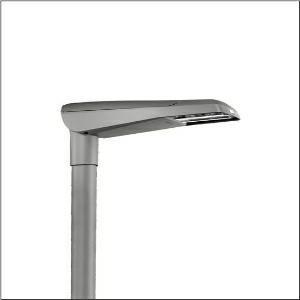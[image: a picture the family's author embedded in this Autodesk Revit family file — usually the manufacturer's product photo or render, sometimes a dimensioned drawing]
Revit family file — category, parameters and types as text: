
# Revit family: streetlight_sl_11_iq_micro___st1_2a_5xc1a41f08ce_4ecf
name_source: partatom
category: Lighting Fixtures
units: mm (PartAtom-declared; Revit-internal decimal feet)

## family parameters
Cut with Voids When Loaded = No
Host = Face
Light Source = No
Part Type = Normal
Room Calculation Point = No
Round Connector Dimension = Use Diameter
Shared = No

## types (1)
- --- (1 x LED, 1960 lm, 12.6 W, 4000K)
    Apparent Load = 13 VA
    CIE Flux Codes = 33 71 96 100 100
    Color Rendering = 70
    Color Temperature = 4000K
    Default Elevation = 1800 mm
    Description = Streetlight SL 11 iQ micro, mast luminaire, primary light control with 3 zone facetted reflector, of plastic, silver coated, highly specular, primary optical cover: cover, of PMMA, transparent, light distribution: ST1.2a, light emission: direct distribution, primary light characteristic: asymmetric, installation type: post-top, side-entry, lamps: LED, High Power LED, rated values: 1.960lm | 12,6W | 155,6lm/W (begin service life); end service life: 1.960lm | 12,9W; at 50% lumin. flux: 980lm | 6,8W | 144,1lm/W, colour temperature: 4000K, colour rendering: CRI > 70, light colour: 740, light setting 1 begin service life: 100% | 1.960lm | 12,6W | 155,6lm/W | 4.000K, light setting 1 end service life: 12,9W, further light settings possible, control: Street-Remote, optimised constant luminous flux control (CLO 2.0), Desk-Remote (wireless, voltage-free reading and setting of iQ features in the workshop via application-optimized NFC function/RFID function), Light-Fading, Smart-Wire, Night-Set, Lumen-Switch, Temp-Guard, Auto-Match, with cable H07RN-F 5x 1.5mm², mains connection: 230..240V, AC, 50/60Hz, connection cable pre-assembled, cable length: 5,5m, luminaire housing, of diecast aluminium, powder-coated, Siteco® metallic grey (DB 702S), please order mast flange separately, inclination adjustable without tools: 0°, 5°, 10°, 15° (post-top) | 0°, -5°, -10°, -15° (side-entry), sealing non-destructively replaceable, multi-level sealing system, length: 600mm, width: 174mm, height: 116mm, mast flange for spigot size: 42mm (side-entry): 5XC10008XM4, 60/48mm (side-entry/post-top): 5XC10108XM2, 76/60mm (side-entry/post-top): 5XC10108XM1, equipment: standard, protection rating (complete): IP66, insulation class (complete): insulation class II (safety insulation), certification: CE, ENEC, ENEC+, VDE, impact resistance: IK10, permissible operating ambient temperature for outdoor applications: -25..+50°C, standard-compliant lighting for roads and squares, Environmental Product Declaration (EPD) tested and certified by an independent institute, packaging unit: 1 piece

Light Distribution: ST1.2a
    Height = 116 mm
    Lamp = 1 x LED
    Lamp Light Flux = 1960 lm
    Lamp Power = 12.6 W
    Lamp count = 1
    Length = 600 mm
    Luminous efficacy = 156 lm/W
    Manufacturer = Siteco
    ModVariant = No
    Model = 5XC1A41F08CE
    Number of Poles = 1
    OnlyDefault = Yes
    Power Factor = 1
    Product Name = Streetlight SL 11 iQ micro | ST1.2a
    Product group = mast luminaire | pylon top
    ProductGroupID = 6100
    Protection Class = Protection class II
    Protection Degree = IP 66
    RLX_Detail_Level = 1
    RLX_Emergency_Light_Flux = 0 lm
    RLX_Emergency_Type = 0
    RLX_Emergency_Type_DB = No
    RlxData = <blob elided: 26497 chars, md5=bde543c6>
    Socket = socket
    Standby Power = 0 W
    System Light Flux = 1960 lm
    System Power = 13 W
    Type Comments = factory setting: luminous flux: 100 % | dim-lin: 254 | 229 mA
    Type Image = l_1006566.jpg
    URL = http://relux.com
    VarID = @adj_018081
    Voltage = 0 V
    Weight = 0.00 kg
    Width = 174 mm

## geometry (parser evidence)
native form markers: Blend x4, Sweep x9
no freeform markers — native parametric forms only
